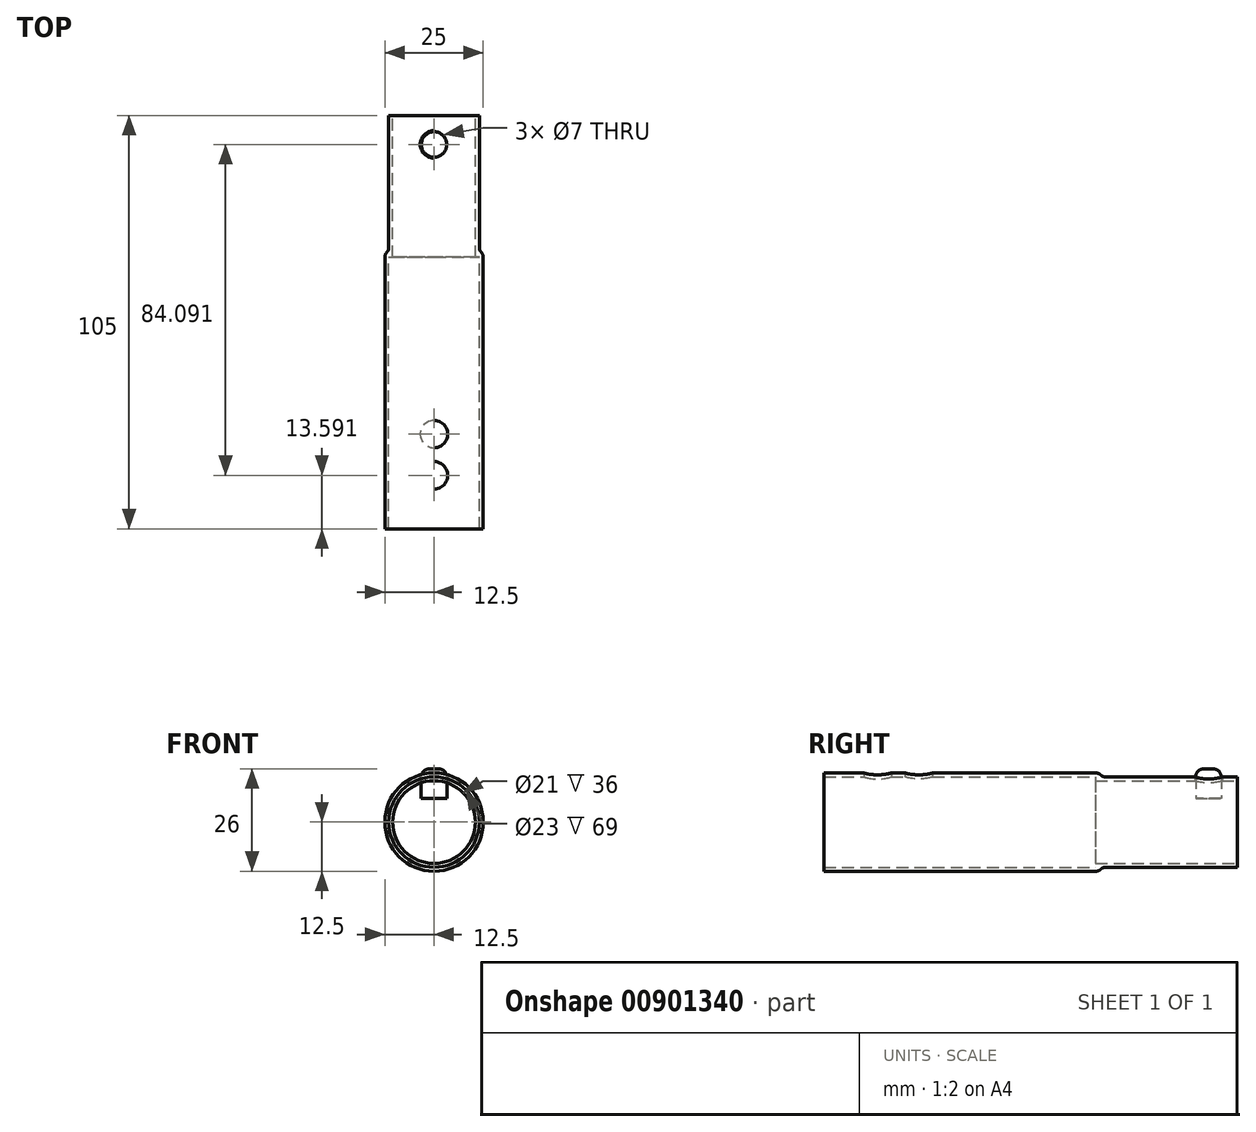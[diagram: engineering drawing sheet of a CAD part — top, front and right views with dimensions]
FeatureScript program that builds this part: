
annotation { "Feature Type Name" : "Feature", "Feature Type Description" : "" }
export const myFeature = defineFeature(function(context is Context, id is Id, definition is map)
    precondition{}
    {
        {
            var Q0;
            Q0=qCreatedBy(makeId("Right.planeOp"),FACE);
            var sketch = newSketch(context, id + "F0", { "sketchPlane" : qUnion([Q0])});
            skLineSegment(sketch, "E0", {"start": v(-61.07, 0) * mm, "end": v(-61.07, 12.5) * mm});
            skLineSegment(sketch, "E1", {"start": v(-61.07, 12.5) * mm, "end": v(8.93, 12.5) * mm});
            skLineSegment(sketch, "E2", {"start": v(8.93, 11.5) * mm, "end": v(8.93, 12.5) * mm});
            skLineSegment(sketch, "E3", {"start": v(8.93, 11.5) * mm, "end": v(43.93, 11.5) * mm});
            skLineSegment(sketch, "E4", {"start": v(43.93, 11.5) * mm, "end": v(43.93, 0) * mm});
            skLineSegment(sketch, "E5", {"start": v(43.93, 0) * mm, "end": v(-61.07, 0) * mm});
            skSolve(sketch);
        }
        {
            var Q0;
            Q0=makeQuery(id+"F0.imprint","IMPRINT",FACE,{"disambiguationData":[TD([[makeQuery(id+"F0.imprint","IMPRINT",EDGE,{"derivedFrom":sQuery(id+"F0.wireOp",EDGE,"xHVXTrwY-pEAa-fC9c-rWHU-DwM3t86Bo6yL")}),1.0]])]});
            var Q1;
            Q1=makeQuery(id+"F0.imprint","IMPRINT",FACE,{"disambiguationData":[TD([[makeQuery(id+"F0.imprint","IMPRINT",EDGE,{"derivedFrom":sQuery(id+"F0.wireOp",EDGE,"E0")}),-1.0]])]});
            var Q2;
            Q2=sQuery(id+"F0.wireOp",EDGE,"E5");
            revolve(context, id + "F1", {"surfaceOperationType" : NewSurfaceOperationType.NEW, "entities" : qUnion([Q0, Q1]), "axis" : qUnion([Q2]), "revolveType" : RevolveType.FULL});
        }
        {
            var Q0;
            Q0=makeQuery(id+"F1.opRevolve","SWEPT_FACE",FACE,{"disambiguationData":[OSD([sQuery(id+"F0.wireOp",EDGE,"E0")])]});
            var Q1;
            Q1=makeQuery(id+"F1.opRevolve","SWEPT_FACE",FACE,{"disambiguationData":[OSD([sQuery(id+"F0.wireOp",EDGE,"X0vb0yjU-hoeb-TaO4-NRRC-7bvT5F4Bvk7U")])]});
            var Q2;
            Q2=makeQuery(id+"F1.opRevolve","SWEPT_FACE",FACE,{"disambiguationData":[OSD([sQuery(id+"F0.wireOp",EDGE,"E4")])]});
            shell(context, id + "F2", {"entities" : qUnion([Q0, Q1, Q2]), "thickness" : 1 * mm});
        }
        {
            var Q0;
            Q0=makeQuery(id+"F1.opRevolve","SWEPT_EDGE",EDGE,{"disambiguationData":[OSD([sQuery(id+"F0.wireOp",EDGE,"E2"),sQuery(id+"F0.wireOp",EDGE,"E3")])]});
            fillet(context, id + "F3", {"entities" : qUnion([Q0]), "radius" : 1.5 * mm, "tangentPropagation" : true, "allowEdgeOverflow" : false});
        }
        {
            var Q0;
            Q0=makeQuery(id+"F3.opFillet","BLEND_EDGE",EDGE,{"blendedFrom":[makeQuery(id+"F1.opRevolve","SWEPT_EDGE",EDGE,{"disambiguationData":[OSD([sQuery(id+"F0.wireOp",EDGE,"fXMVCEnT-Ex3i-Xaum-mOsN-Bt5lRMQ2mptr"),sQuery(id+"F0.wireOp",EDGE,"E2")])]}),makeQuery(id+"F1.opRevolve","SWEPT_FACE",FACE,{"disambiguationData":[OSD([sQuery(id+"F0.wireOp",EDGE,"E1")])]})],"blendedInto":[makeQuery(id+"F1.opRevolve","SWEPT_FACE",FACE,{"disambiguationData":[OSD([sQuery(id+"F0.wireOp",EDGE,"E1")])]})]});
            fillet(context, id + "F4", {"entities" : qUnion([Q0]), "radius" : 2 * mm, "tangentPropagation" : true, "allowEdgeOverflow" : false});
        }
        {
            var Q0;
            Q0=qCreatedBy(makeId("Top.planeOp"),FACE);
            var sketch = newSketch(context, id + "F5", { "sketchPlane" : qUnion([Q0])});
            skLineSegment(sketch, "E6", {"start": v(0, 51.61) * mm, "end": v(0, 36.61) * mm});
            skCircle(sketch, "E7", {"center": v(0, 36.61) * mm, "radius": 3.5 * mm});
            skLineSegment(sketch, "E8", {"start": v(0, -60.98) * mm, "end": v(0, -36.98) * mm});
            skCircle(sketch, "E9", {"center": v(0, -36.98) * mm, "radius": 3.5 * mm});
            skCircle(sketch, "E10", {"center": v(0, -36.98) * mm, "radius": 3.25 * mm});
            skCircle(sketch, "E11", {"center": v(0, 36.61) * mm, "radius": 3.25 * mm});
            skCircle(sketch, "E12", {"center": v(0, -47.48) * mm, "radius": 3.5 * mm});
            skSolve(sketch);
        }
        {
            var Q0;
            Q0=makeQuery(id+"F5.imprint","IMPRINT",FACE,{"disambiguationData":[TD([[makeQuery(id+"F5.imprint","IMPRINT",EDGE,{"derivedFrom":sQuery(id+"F5.wireOp",EDGE,"E9")}),1.0]])]});
            var Q1;
            Q1=makeQuery(id+"F5.imprint","IMPRINT",FACE,{"disambiguationData":[TD([[makeQuery(id+"F5.imprint","IMPRINT",EDGE,{"derivedFrom":sQuery(id+"F5.wireOp",EDGE,"E7")}),1.0]])]});
            var Q2;
            Q2=makeQuery(id+"F5.imprint","IMPRINT",FACE,{"disambiguationData":[TD([[makeQuery(id+"F5.imprint","IMPRINT",EDGE,{"derivedFrom":sQuery(id+"F5.wireOp",EDGE,"E11")}),1.0]])]});
            var Q3;
            Q3=makeQuery(id+"F5.imprint","IMPRINT",FACE,{"disambiguationData":[TD([[makeQuery(id+"F5.imprint","IMPRINT",EDGE,{"derivedFrom":sQuery(id+"F5.wireOp",EDGE,"E10")}),1.0]])]});
            var Q4;
            {var subQ0=sQuery(id+"F5.wireOp",EDGE,"E12");var subQ1=sQuery(id+"F5.wireOp",EDGE,"E8");var subQ2=makeQuery(id+"F5.imprint","INTERSECT",VERTEX,{"disambiguationData":[OD(0.0)],"derivedFrom":[subQ1,subQ0]});Q4=makeQuery(id+"F5.imprint","IMPRINT",FACE,{"disambiguationData":[TD([[makeQuery(id+"F5.imprint","IMPRINT",EDGE,{"disambiguationData":[TD([[subQ2,-1.0]])],"derivedFrom":subQ1}),-1.0]])]});}
            var Q5;
            {var subQ0=sQuery(id+"F5.wireOp",EDGE,"E12");var subQ1=sQuery(id+"F5.wireOp",EDGE,"E8");var subQ2=makeQuery(id+"F5.imprint","INTERSECT",VERTEX,{"disambiguationData":[OD(0.0)],"derivedFrom":[subQ1,subQ0]});Q5=makeQuery(id+"F5.imprint","IMPRINT",FACE,{"disambiguationData":[TD([[makeQuery(id+"F5.imprint","IMPRINT",EDGE,{"disambiguationData":[TD([[subQ2,-1.0]])],"derivedFrom":subQ1}),1.0]])]});}
            extrude(context, id + "F6", {"entities" : qUnion([Q0, Q1, Q2, Q3, Q4, Q5]), "operationType" : NewBodyOperationType.REMOVE, "depth" : 15 * mm, "offsetDistance" : 25 * mm});
        }
        {
            var Q0;
            Q0=qCreatedBy(makeId("Top.planeOp"),FACE);
            cPlane(context, id + "F7", {"entities" : qUnion([Q0]), "cplaneType" : CPlaneType.OFFSET, "offset" : 6 * mm, "width" : 150 * mm, "height" : 150 * mm});
        }
        {
            var Q0;
            Q0=qCreatedBy(id+"F7.planeOp",FACE);
            var sketch = newSketch(context, id + "F8", { "sketchPlane" : qUnion([Q0])});
            skCircle(sketch, "E13", {"center": v(0, 36.6) * mm, "radius": 3.25 * mm});
            skSolve(sketch);
        }
        {
            var Q0;
            Q0=makeQuery(id+"F8.imprint","IMPRINT",FACE,{"disambiguationData":[TD([[makeQuery(id+"F8.imprint","IMPRINT",EDGE,{"derivedFrom":sQuery(id+"F8.wireOp",EDGE,"E13")}),1.0]])]});
            extrude(context, id + "F9", {"entities" : qUnion([Q0]), "depth" : 7.5 * mm, "offsetDistance" : 25 * mm});
        }
        {
            var Q0;
            Q0=makeQuery(id+"F9.opExtrude","CAP_FACE",FACE,{"disambiguationData":[OSD([sQuery(id+"F8.wireOp",EDGE,"E13")])],"isStart":false});
            fillet(context, id + "F10", {"entities" : qUnion([Q0]), "radius" : 2 * mm, "tangentPropagation" : true, "allowEdgeOverflow" : false});
        }
    });
